# Revit family: QF_COLDLINE_W14F
name_source: partatom
category: Specialty Equipment
revit_build: Autodesk Revit 2018 (Build: 20170223_1515(x64)
units: mm (PartAtom-declared; Revit-internal decimal feet)

## family parameters
Always vertical = Yes
Cut with Voids When Loaded = No
Part Type = Normal
Room Calculation Point = No
Round Connector Dimension = Use Diameter
Shared = No
Work Plane-Based = No

## types (1)
- H 1778 mm_W64143000001 - Vision F blast chiller -40°+65°C 14 trays GN-EN plug-in air unit
    Absorbed Current = 13,12 A
    Accessory = No
    Apparent Power = 220 VA
    Assembly Code = W64143000001
    Castor Roller = Roller Castor
    Climate Class = 5
    Conn Conduit = No
    Cooling capacity = 5440 W
    Cooling gas = R452A
    Cycle = 50 Hz
    Defrost = Hot gas
    Depth Actual = 797 mm  [stored 2.61483 ft]
    Depth of Table = 797 mm  [stored 2.61483 ft]
    Description = Vision F blast chiller -40°+65°C 14 trays GN-EN plug-in air unit
    Dimension = 780×859×1778 mm
    Door 2 = Door Left : Single
    Electric power = 406 W
    Glaze Frame Width = 80 mm  [stored 0.262467 ft]
    Gross Capacity = 463 lt
    Height Actual = 1778 mm  [stored 5.83333 ft]
    Humidifier = Included
    Humidity range = 45% - 95% with humidifier
    Length Actual = 780 mm  [stored 2.55906 ft]
    Length of Table = 780 mm  [stored 2.55906 ft]
    Main switch integrated = No
    Manufacturer = Coldline
    Max capacity = 23 trays GN1/1, EN60x40 h 20 mm
    Model = W14F
    National Water Regulation Certification = No
    No Load Power Draw = No
    Number of Poles = 1
    Odor Trap Included = No
    Operational Current = 1 A
    Packing dimensions = 875×915×1820 mm
    Phase = 1
    Potential Equalisation = No
    Refrigerant Compressor Remote = No
    Refrigeration Defrost Drain = No
    Refrigerent Unit = Plug In
    Start Up Current = 1 A
    Table Height = 1638 mm  [stored 5.37402 ft]
    Table L Top = No
    Table L top = 138 mm
    Table Top = 40 mm  [stored 0.131234 ft]
    Table Top Plain = Yes
    Temp. Range = -40°+65°C
    Top = 4 cm thickness
    Total rate = 5200 W
    URL Cutsheet = https://coldline.it
    URL Manufacturer = https://coldline.it
    Valve = Electronic expansion valve
    Ventilation range = 25% - 100%
    Volt Free Conn = No
    Voltage = 400-415 V - 50-60 Hz
    Volts = 240 V
    Weight = 205.00 kg
    Width Of Door = 713 mm
    Yield +90 / +3 = 70 Kg
    Yield +90 / -18 = 56 Kg

note: [stored X ft] marks values corroborated as IEEE doubles in the binary element streams (Revit-internal decimal feet)

## geometry (parser evidence)
native form markers: Sweep x32
no freeform markers — native parametric forms only
